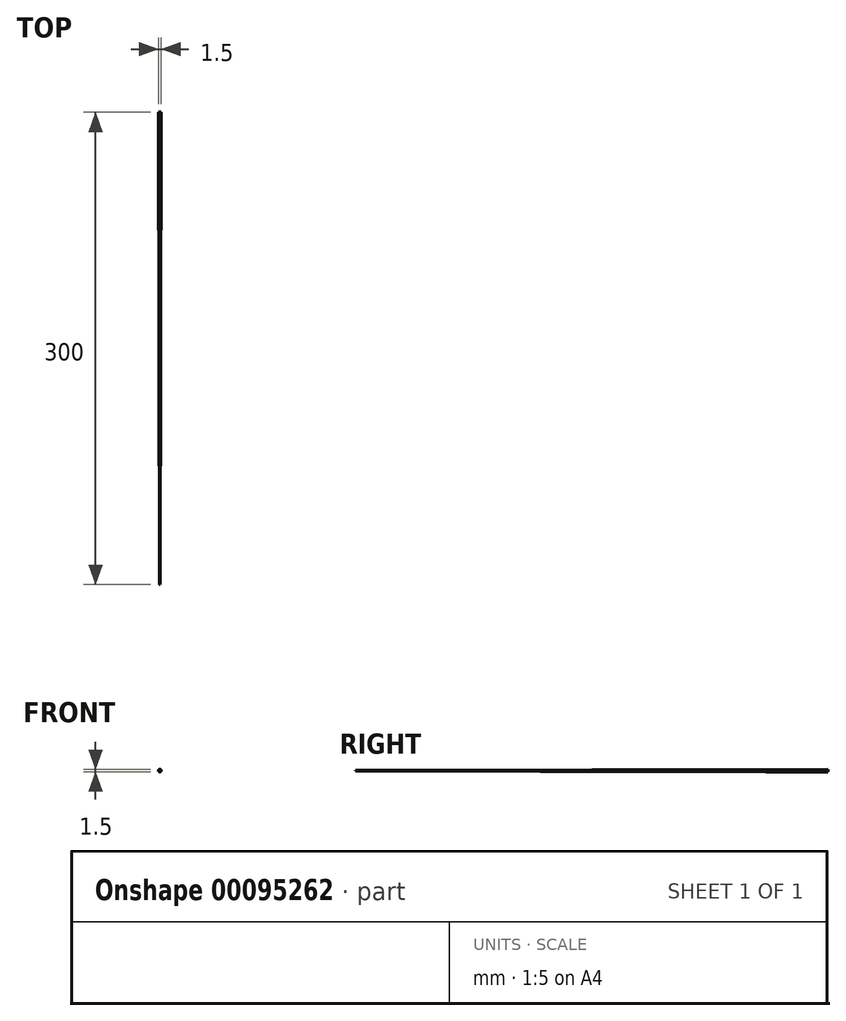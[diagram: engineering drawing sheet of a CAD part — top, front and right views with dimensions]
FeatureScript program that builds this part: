
annotation { "Feature Type Name" : "Feature", "Feature Type Description" : "" }
export const myFeature = defineFeature(function(context is Context, id is Id, definition is map)
    precondition{}
    {
        {
            var Q0;
            Q0=qCreatedBy(makeId("Front.planeOp"),FACE);
            var sketch = newSketch(context, id + "F0", { "sketchPlane" : qUnion([Q0])});
            skCircle(sketch, "E0", {"center": v(0, 0) * mm, "radius": 0.75 * mm});
            skSolve(sketch);
        }
        {
            var Q0;
            Q0=qCreatedBy(makeId("Front.planeOp"),FACE);
            cPlane(context, id + "F1", {"entities" : qUnion([Q0]), "cplaneType" : CPlaneType.OFFSET, "offset" : 300 * mm, "width" : 150 * mm, "height" : 150 * mm});
        }
        {
            var Q0;
            Q0=qCreatedBy(id+"F1.planeOp",FACE);
            var sketch = newSketch(context, id + "F2", { "sketchPlane" : qUnion([Q0])});
            skCircle(sketch, "E1", {"center": v(0, 0) * mm, "radius": 0.1 * mm});
            skSolve(sketch);
        }
        {
            var Q0;
            Q0 = qSketchRegion(id + "F0", true);
            var Q1;
            Q1 = qSketchRegion(id + "F2", true);
            loft(context, id + "F3", {"sheetProfilesArray" : [{ "sheetProfileEntities" : qUnion([Q0]) }, { "sheetProfileEntities" : qUnion([Q1]) }]});
        }
    });
